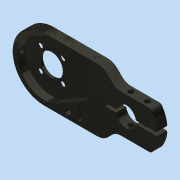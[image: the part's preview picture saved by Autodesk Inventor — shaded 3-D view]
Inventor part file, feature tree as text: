
AUTODESK INVENTOR PART (.ipt)
format: ipt  version: 2015 (Build 190159000, 159)  size: 305,152 bytes
history: native  units: in
note: dims shown in document units (in); Inventor stores cm internally (conversion verified against a paired STEP export)
features: sketch x8, extrude x8, projected_geometry x4, thread x3, mirror x1, plane x1, chamfer x1
ambient origin geometry x8: Origin, YZ Plane, XZ Plane, XY Plane, X Axis, Y Axis, Z Axis, Center Point
bodies: Body1 (feature_tree)
feature tree (26):
  sketch  "Sketch1"  dims[d0=0.748in d1=2.3622in]
  extrude  "Extrusion4"  Depth=2.3622in
  extrude  "Extrusion6"  Depth=3.079in
  extrude  "Extrusion7"  Depth=0.1654in
  extrude  "Extrusion8"  Depth=0.1654in
  thread  "Thread2"  [1 undecoded]
  mirror  "Mirror1"
  plane  "Work Plane2"
  extrude  "Extrusion9"  Depth=0.1181in
  extrude  "Extrusion10"  Depth=0.0591in
  chamfer  "Chamfer1"  [1 undecoded]
  extrude  "Extrusion11"  Depth=0.126in
  extrude  "Extrusion12"  Depth=0.126in
  thread  "Thread1"  [1 undecoded]
  thread  "Thread3"  [1 undecoded]
  sketch  "Sketch4"  dims[d2=0.8465in d3=3.079in]
  sketch  "Sketch5"  dims[d4=2.3622in d5=0.1654in]
  sketch  "Sketch6"  dims[d6=0.1654in d7=0.1654in d8=0.1654in]
  projected_geometry  "Projected Loop3"
  sketch  "Sketch7"  dims[d9=1.1811in d13=0.1181in]
  projected_geometry  "Projected Loop4"
  sketch  "Sketch8"  dims[d20=0.1181in d21=0.0591in]
  projected_geometry  "Projected Loop5"
  projected_geometry  "Projected Loop6"
  sketch  "Sketch9"  dims[d22=0.7874in]
  sketch  "Sketch10"  dims[d23=0.375in d24=0.0in d28=2.0079in d29=1.9685in d30=0.3125in d31=0.2812in d32=0.0in d34=0.125in d35=1.1811in d36=1.1811in d38=0.376in d39=0.376in d41=1.1811in d43=0.125in d44=0.375in d45=0.125in d47=0.2812in d48=0.0in d49=0.0625in d50=0.159in d51=0.1875in d52=0.5in d53=0.0in d54=0.159in d55=0.5in d56=0.0in d57=0.25in d58=0.25in d59=0.25in d60=1.0in d61=0.0in d62=0.0807in d63=0.125in d64=45.0deg d65=0.6772in d66=2.3307in d67=0.315in d68=0.126in d69=0.126in d70=0.0787in d71=0.4331in d72=1.0in d73=0.0in d74=0.0984in d75=1.0in d76=0.0in d77=1.0in d78=0.0in d79=1.0in d80=0.0in d81=1.0in d82=0.0in d84=0.0312in d85=0.1875in d86=0.201in d87=0.201in]
note: 4 required parameter values undecoded (feature->parameter linkage not recoverable at this tier; creation-order binding heuristic only, values carry confidence <= 0.55)
